# Revit family: Rohrschelle Maxima PSM, M 8-M10 ,Ø 12- 76, o.D
name_source: partatom
category: HLS-Bauteile
revit_build: Autodesk Revit 2017 (Build: 20190507_1515(x64)
units: mm (PartAtom-declared; Revit-internal decimal feet)

## family parameters
Arbeitsebenenbasiert = Ja
Beim Laden mit Abzugskörper schneiden = Nein
Bemaßung runder Anschluss = Durchmesser verwenden
Gemeinsam genutzt = Ja
Immer vertikal = Nein
Raumberechnungspunkt = Nein
Teiletyp = Normal

## types (11) — shared parameters
A = 25 mm  [stored 0.082021 ft]
Anschluss = M8/M10
Bauart = zweiteilig
Brandschutz = RAL-GZ 656
DF1 = 24 mm  [stored 0.0787402 ft]
DF2 = 23 mm  [stored 0.0754593 ft]
DVS = 15 mm  [stored 0.0492126 ft]
Fabrikat = MEFA
Firma = MEFA Befestigungs- und Montagesysteme GmbH
HGA = 22 mm  [stored 0.0721785 ft]
Kurztext1 = Rohrschelle Maxima PSM 25x3,0
MB = 25 mm  [stored 0.082021 ft]
MD = 3 mm  [stored 0.00984252 ft]
Material = Stahl
Materialmaße = 25x3,0 mm
Materialname = S235
Mengeneinheit = St
Oberflaeche = galvanisch verzinkt
Verschluss = Pendelsteckmuttern
Verschluss-Schraube = M8
Vorgabe-Ansicht = 1219 mm
max. zul. Last = 3.00 kN
max. zul. Last horizontal = 0.00 kN
max. zul. Last vertikal = 0.00 kN
vpe = 1 St
zero-valued in all types: Nennweite DN Rohr, Rohraußendurchmesser, Stärke Material

## per-type parameters (varying)
| type | AB | Achsabstand | Anschlußhöhe | Artikelnummer | B | Breite | D | Dmax | Dmin | EAN | Gewicht | Gewicht pro Bauteil | H | Kurztext2 | R | RM | Rohraußendurchmesser Zoll | S | max. Höhe | max. Rohraußendurchmesser | min. Rohraußendurchmesser |
| Maxima PSM, M8/M10, Ø 12- 16, o.D. | 4 mm  [stored 0.0131234 ft] | 45 mm | 19 mm | 0068835 | 69 mm | 69 mm | 16 mm  [stored 0.0524934 ft] | 16 mm  [stored 0.0524934 ft] | 12 mm  [stored 0.0393701 ft] | 4250928402394 | 0.16 kg | 0.16 kg | 44 mm | 12 - 16 mm M8/M10 | 8 mm  [stored 0.0262467 ft] | 11 mm  [stored 0.0360892 ft] | Zoll | 45 mm  [stored 0.147638 ft] | 43 mm  [stored 0.141076 ft] | 16 mm  [stored 0.0524934 ft] | 12 mm  [stored 0.0393701 ft] |
| Maxima PSM, M8/M10, Ø 17- 19, o.D. | 2 mm  [stored 0.00656168 ft] | 48 mm | 24 mm | 00688612 | 72 mm | 72 mm | 19 mm  [stored 0.062336 ft] | 19 mm  [stored 0.062336 ft] | 17 mm | 4250928402462 | 0.17 kg | 0.17 kg | 47 mm | 17 - 19 mm M8/M10 | 10 mm  [stored 0.0328084 ft] | 13 mm | Zoll | 48 mm | 46 mm  [stored 0.150919 ft] | 19 mm  [stored 0.062336 ft] | 17 mm |
| Maxima PSM, M8/M10, Ø 20- 23, o.D. | 3 mm  [stored 0.00984252 ft] | 52 mm | 24 mm | 0068838 | 76 mm | 76 mm | 23 mm  [stored 0.0754593 ft] | 23 mm  [stored 0.0754593 ft] | 20 mm  [stored 0.0656168 ft] | 4250928402424 | 0.17 kg | 0.17 kg | 51 mm | 20 - 23 mm M8/M10 | 12 mm  [stored 0.0393701 ft] | 15 mm  [stored 0.0492126 ft] | 1/2 Zoll | 52 mm | 50 mm | 23 mm  [stored 0.0754593 ft] | 20 mm  [stored 0.0656168 ft] |
| Maxima PSM, M8/M10, Ø 25- 29, o.D. | 4 mm  [stored 0.0131234 ft] | 58 mm | 24 mm | 0068837 | 82 mm | 82 mm | 29 mm  [stored 0.0951444 ft] | 29 mm  [stored 0.0951444 ft] | 25 mm  [stored 0.082021 ft] | 4250928402417 | 0.18 kg | 0.18 kg | 57 mm | 25 - 29 mm M8/M10 | 15 mm  [stored 0.0492126 ft] | 18 mm  [stored 0.0590551 ft] | 3/4 Zoll | 58 mm | 56 mm | 29 mm  [stored 0.0951444 ft] | 25 mm  [stored 0.082021 ft] |
| Maxima PSM, M8/M10, Ø 30- 35, o.D. | 5 mm  [stored 0.0164042 ft] | 64 mm | 24 mm | 0068836 | 88 mm | 88 mm | 35 mm  [stored 0.114829 ft] | 35 mm  [stored 0.114829 ft] | 30 mm  [stored 0.0984252 ft] | 4250928402400 | 0.19 kg | 0.19 kg | 63 mm | 32 - 35 mm M8/M10 | 18 mm  [stored 0.0590551 ft] | 21 mm  [stored 0.0688976 ft] | 1 Zoll | 64 mm | 62 mm | 35 mm  [stored 0.114829 ft] | 32 mm  [stored 0.104987 ft] |
| Maxima PSM, M8/M10, Ø 36- 40, o.D. | 4 mm  [stored 0.0131234 ft] | 69 mm | 24 mm | 0068841 | 93 mm | 93 mm | 40 mm  [stored 0.131234 ft] | 40 mm  [stored 0.131234 ft] | 36 mm  [stored 0.11811 ft] | 4250928402431 | 0.20 kg | 0.20 kg | 68 mm | 36 - 40 mm M8/M10 | 20 mm  [stored 0.0656168 ft] | 23 mm  [stored 0.0754593 ft] | Zoll | 69 mm | 67 mm | 40 mm  [stored 0.131234 ft] | 36 mm  [stored 0.11811 ft] |
| Maxima PSM, M8/M10, Ø 41- 46, o.D. | 5 mm  [stored 0.0164042 ft] | 75 mm | 24 mm | 0068847 | 99 mm | 99 mm | 46 mm  [stored 0.150919 ft] | 46 mm  [stored 0.150919 ft] | 41 mm  [stored 0.134514 ft] | 4250928402448 | 0.21 kg | 0.21 kg | 74 mm | 41 - 46 mm M8/M10 | 23 mm  [stored 0.0754593 ft] | 26 mm  [stored 0.0853018 ft] | 1 1/4 Zoll | 75 mm | 73 mm | 46 mm  [stored 0.150919 ft] | 41 mm  [stored 0.134514 ft] |
| Maxima PSM, M8/M10, Ø 48- 55, o.D. | 7 mm  [stored 0.0229659 ft] | 84 mm | 24 mm | 0068856 | 108 mm | 108 mm | 55 mm | 55 mm | 48 mm | 4250928402455 | 0.23 kg | 0.23 kg | 83 mm | 48 - 55 mm M8/M10 | 28 mm | 31 mm | 1 1/2 Zoll | 84 mm | 82 mm | 55 mm | 48 mm |
| Maxima PSM, M8/M10, Ø 57- 61, o.D. | 4 mm  [stored 0.0131234 ft] | 90 mm | 24 mm | 0068863 | 114 mm | 114 mm | 61 mm | 61 mm | 57 mm | 4250928402479 | 0.24 kg | 0.24 kg | 89 mm | 57 - 61 mm M8/M10 | 31 mm | 34 mm | 2 Zoll | 90 mm | 88 mm | 61 mm | 57 mm |
| Maxima PSM, M8/M10, Ø 63- 67, o.D. | 4 mm  [stored 0.0131234 ft] | 96 mm | 24 mm | 0068882 | 120 mm | 120 mm | 67 mm | 67 mm | 63 mm | 4250928402561 | 0.25 kg | 0.25 kg | 95 mm | 63 - 67 mm M8/M10 | 34 mm | 37 mm  [stored 0.121391 ft] | Zoll | 96 mm | 94 mm | 67 mm | 63 mm |
| Maxima PSM, M8/M10, Ø 70- 76, o.D. | 6 mm  [stored 0.019685 ft] | 105 mm | 24 mm | 00880769 | 129 mm | 129 mm | 76 mm | 76 mm | 70 mm | 4250928407269 | 0.27 kg | 0.27 kg | 104 mm | 70 - 76 mm M8/M10 | 38 mm  [stored 0.124672 ft] | 41 mm  [stored 0.134514 ft] | 2 1/2 Zoll | 105 mm | 103 mm | 76 mm | 70 mm |

note: [stored X ft] marks values corroborated as IEEE doubles in the binary element streams (Revit-internal decimal feet)

## geometry (parser evidence)
native form markers: Sweep x2
no freeform markers — native parametric forms only
